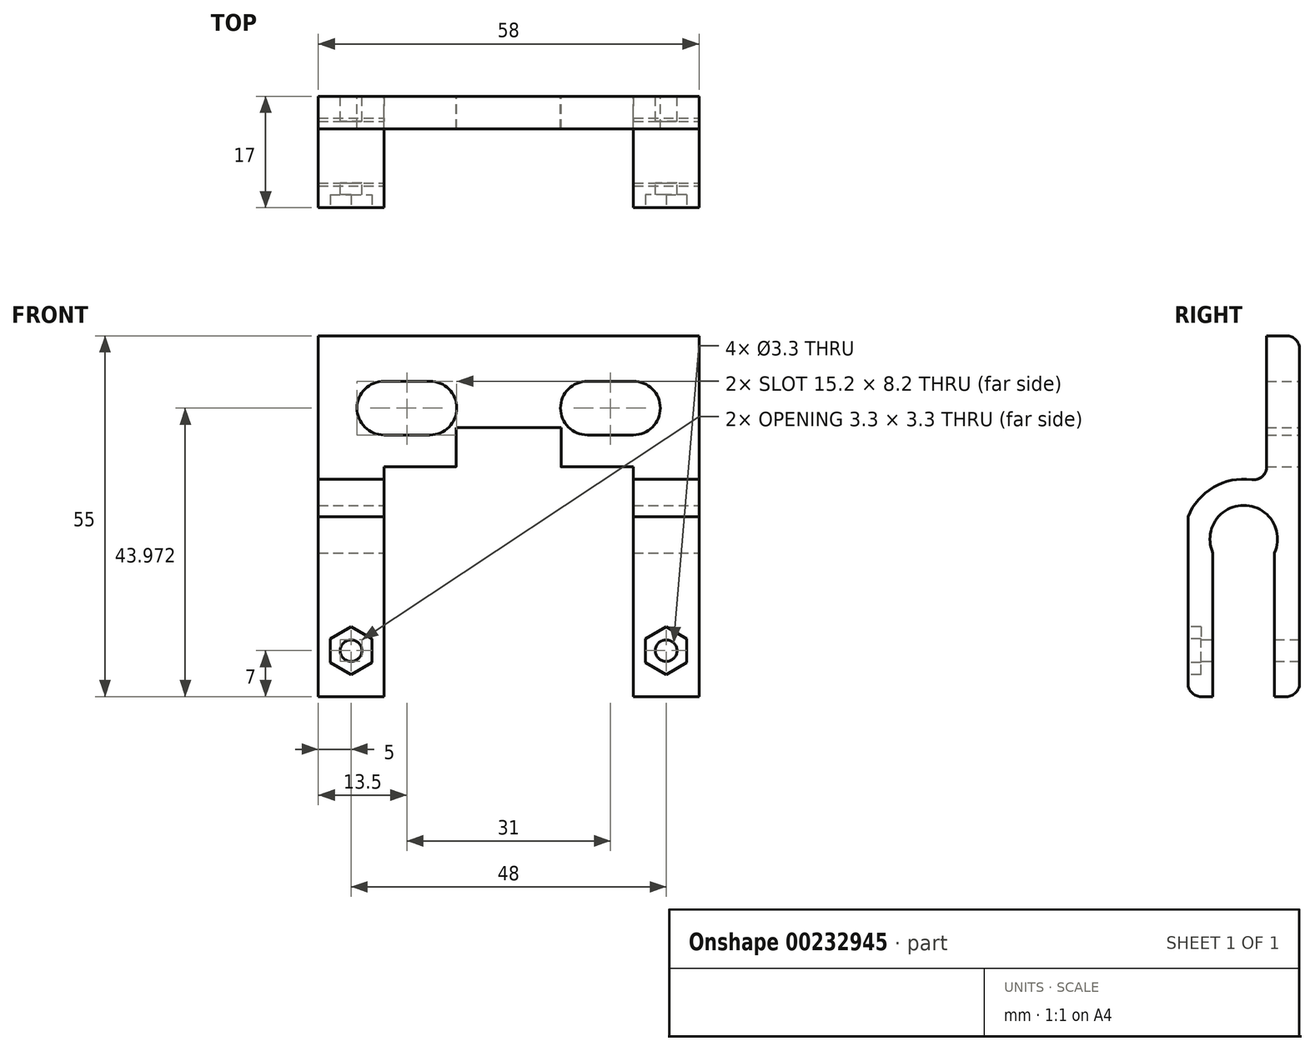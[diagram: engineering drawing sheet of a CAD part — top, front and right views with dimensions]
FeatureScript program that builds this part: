
annotation { "Feature Type Name" : "Feature", "Feature Type Description" : "" }
export const myFeature = defineFeature(function(context is Context, id is Id, definition is map)
    precondition{}
    {
        {
            var Q0;
            Q0=qCreatedBy(makeId("Front.planeOp"),FACE);
            var sketch = newSketch(context, id + "F0", { "sketchPlane" : qUnion([Q0])});
            skLineSegment(sketch, "E0.bottom", {"start": v(-13, -25) * mm, "end": v(-3, -25) * mm});
            skLineSegment(sketch, "E0.left", {"start": v(-13, -25) * mm, "end": v(-13, 25) * mm});
            skLineSegment(sketch, "E1", {"start": v(-3, -25) * mm, "end": v(-3, -5) * mm});
            skLineSegment(sketch, "E2", {"start": v(35, -5) * mm, "end": v(35, -25) * mm});
            skLineSegment(sketch, "E3", {"start": v(35, -25) * mm, "end": v(45, -25) * mm});
            skLineSegment(sketch, "E4", {"start": v(45, -25) * mm, "end": v(45, 25) * mm});
            skLineSegment(sketch, "E5", {"start": v(45, 25) * mm, "end": v(45, 30) * mm});
            skLineSegment(sketch, "E6", {"start": v(45, 30) * mm, "end": v(-13, 30) * mm});
            skLineSegment(sketch, "E7", {"start": v(-13, 30) * mm, "end": v(-13, 25) * mm});
            skLineSegment(sketch, "E8", {"start": v(-3, -5) * mm, "end": v(-3, 0) * mm});
            skLineSegment(sketch, "E9", {"start": v(35, 0) * mm, "end": v(35, -5) * mm});
            skLineSegment(sketch, "E10", {"start": v(-13, 30) * mm, "end": v(-13, 18.97) * mm});
            skPoint(sketch, "E11", {"position": v(4, 18.97) * mm});
            skPoint(sketch, "E12", {"position": v(28, 18.97) * mm});
            skArc(sketch, "E13", {"start": v(28, 23.07) * mm, "mid": v(23.9, 18.97) * mm, "end": v(28, 14.87) * mm});
            skArc(sketch, "E14", {"start": v(-3, 23.07) * mm, "mid": v(-7.1, 18.97) * mm, "end": v(-3, 14.87) * mm});
            skArc(sketch, "E15", {"start": v(35, 14.87) * mm, "mid": v(39.1, 18.97) * mm, "end": v(35, 23.07) * mm});
            skLineSegment(sketch, "E16", {"start": v(4, 14.87) * mm, "end": v(-3, 14.87) * mm});
            skLineSegment(sketch, "E17", {"start": v(-3, 23.07) * mm, "end": v(4, 23.07) * mm});
            skLineSegment(sketch, "E18", {"start": v(28, 14.87) * mm, "end": v(35, 14.87) * mm});
            skLineSegment(sketch, "E19", {"start": v(28, 23.07) * mm, "end": v(35, 23.07) * mm});
            skPoint(sketch, "E20.trimOffspring.end.orphan", {"position": v(45, 18.97) * mm});
            skLineSegment(sketch, "E21", {"start": v(-8, -25) * mm, "end": v(-8, -18) * mm});
            skLineSegment(sketch, "E22", {"start": v(40, -25) * mm, "end": v(40, -18) * mm});
            skCircle(sketch, "E23", {"center": v(40, -18) * mm, "radius": 1.65 * mm});
            skCircle(sketch, "E24", {"center": v(-8, -18) * mm, "radius": 1.65 * mm});
            skCircle(sketch, "E25.cCircle", {"center": v(-8, -18) * mm, "radius": 3.1 * mm, "construction": true});
            skLineSegment(sketch, "E25.0", {"start": v(-4.9, -16.21) * mm, "end": v(-4.9, -19.79) * mm});
            skLineSegment(sketch, "E25.1", {"start": v(-4.9, -19.79) * mm, "end": v(-8, -21.58) * mm});
            skLineSegment(sketch, "E25.2", {"start": v(-8, -21.58) * mm, "end": v(-11.1, -19.79) * mm});
            skLineSegment(sketch, "E25.3", {"start": v(-11.1, -19.79) * mm, "end": v(-11.1, -16.21) * mm});
            skLineSegment(sketch, "E25.4", {"start": v(-11.1, -16.21) * mm, "end": v(-8, -14.42) * mm});
            skLineSegment(sketch, "E25.5", {"start": v(-8, -14.42) * mm, "end": v(-4.9, -16.21) * mm});
            skPoint(sketch, "E25.0.midPoint", {"position": v(-4.9, -18) * mm});
            skCircle(sketch, "E26.cCircle", {"center": v(40, -18) * mm, "radius": 3.1 * mm, "construction": true});
            skLineSegment(sketch, "E26.0", {"start": v(36.9, -19.79) * mm, "end": v(36.9, -16.21) * mm});
            skLineSegment(sketch, "E26.1", {"start": v(36.9, -16.21) * mm, "end": v(40, -14.42) * mm});
            skLineSegment(sketch, "E26.2", {"start": v(40, -14.42) * mm, "end": v(43.1, -16.21) * mm});
            skLineSegment(sketch, "E26.3", {"start": v(43.1, -16.21) * mm, "end": v(43.1, -19.79) * mm});
            skLineSegment(sketch, "E26.4", {"start": v(43.1, -19.79) * mm, "end": v(40, -21.58) * mm});
            skLineSegment(sketch, "E26.5", {"start": v(40, -21.58) * mm, "end": v(36.9, -19.79) * mm});
            skPoint(sketch, "E26.0.midPoint", {"position": v(36.9, -18) * mm});
            skLineSegment(sketch, "E27", {"start": v(-3, 0) * mm, "end": v(-3, 5) * mm});
            skLineSegment(sketch, "E28", {"start": v(35, 5) * mm, "end": v(35, 0) * mm});
            skLineSegment(sketch, "E29", {"start": v(35, 0) * mm, "end": v(35, 10) * mm});
            skLineSegment(sketch, "E30", {"start": v(35, 10) * mm, "end": v(24, 10) * mm});
            skLineSegment(sketch, "E31", {"start": v(-3, 10) * mm, "end": v(-3, 5) * mm});
            skLineSegment(sketch, "E32", {"start": v(24, 10) * mm, "end": v(24, 16) * mm});
            skLineSegment(sketch, "E33", {"start": v(8, 10) * mm, "end": v(8, 16) * mm});
            skLineSegment(sketch, "E34.trimOffspring", {"start": v(24, 16) * mm, "end": v(8, 16) * mm});
            skArc(sketch, "E35", {"start": v(4, 14.87) * mm, "mid": v(8.1, 18.97) * mm, "end": v(4, 23.07) * mm});
            skLineSegment(sketch, "E36.trimOffspring", {"start": v(8, 10) * mm, "end": v(-3, 10) * mm});
            skSolve(sketch);
        }
        {
            var Q0;
            Q0=makeQuery(id+"F0.imprint","IMPRINT",FACE,{"disambiguationData":[TD([[makeQuery(id+"F0.imprint","IMPRINT",EDGE,{"derivedFrom":sQuery(id+"F0.wireOp",EDGE,"E0.left")}),-1.0]])]});
            var Q1;
            Q1=makeQuery(id+"F0.imprint","IMPRINT",FACE,{"disambiguationData":[TD([[makeQuery(id+"F0.imprint","IMPRINT",EDGE,{"derivedFrom":sQuery(id+"F0.wireOp",EDGE,"E23")}),-1.0]])]});
            var Q2;
            Q2=makeQuery(id+"F0.imprint","IMPRINT",FACE,{"disambiguationData":[TD([[makeQuery(id+"F0.imprint","IMPRINT",EDGE,{"derivedFrom":sQuery(id+"F0.wireOp",EDGE,"E24")}),-1.0]])]});
            extrude(context, id + "F1", {"entities" : qUnion([Q0, Q1, Q2]), "depth" : 17 * mm});
        }
        {
            var Q0;
            Q0=makeQuery(id+"F1.opExtrude","SWEPT_FACE",FACE,{"disambiguationData":[OSD([sQuery(id+"F0.wireOp",EDGE,"E4")])]});
            var sketch = newSketch(context, id + "F2", { "sketchPlane" : qUnion([Q0])});
            skArc(sketch, "E37", {"start": v(-3.8, -3.1) * mm, "mid": v(-8.5, 4.15) * mm, "end": v(-13.2, -3.1) * mm});
            skLineSegment(sketch, "E38", {"start": v(-17, -25) * mm, "end": v(-13.2, -25) * mm});
            skLineSegment(sketch, "E39", {"start": v(0, -25) * mm, "end": v(-3.8, -25) * mm});
            skLineSegment(sketch, "E40", {"start": v(-13.2, -25) * mm, "end": v(-13.2, -3.1) * mm});
            skLineSegment(sketch, "E41", {"start": v(-3.8, -25) * mm, "end": v(-3.8, -3.1) * mm});
            skPoint(sketch, "E42.start.orphan", {"position": v(-8.5, -25) * mm});
            skArc(sketch, "E43.0", {"start": v(-5, 7.45) * mm, "mid": v(-12.06, 7.43) * mm, "end": v(-17, 2.39) * mm});
            skPoint(sketch, "E44", {"position": v(-17, 2.39) * mm});
            skLineSegment(sketch, "E45", {"start": v(0, -25) * mm, "end": v(-4, -25) * mm});
            skLineSegment(sketch, "E46", {"start": v(0, 30) * mm, "end": v(-5, 30) * mm});
            skLineSegment(sketch, "E47", {"start": v(-5, 30) * mm, "end": v(-5, 7.45) * mm});
            skPoint(sketch, "E48", {"position": v(0, 18.99) * mm});
            skSolve(sketch);
        }
        {
            var Q0;
            {var subQ0=sQuery(id+"F2.wireOp",EDGE,"E43.0");Q0=makeQuery(id+"F2.imprint","IMPRINT",FACE,{"disambiguationData":[TD([[makeQuery(id+"F2.imprint","IMPRINT",EDGE,{"derivedFrom":subQ0}),-1.0]])]});}
            var Q1;
            Q1=makeQuery(id+"F2.imprint","IMPRINT",FACE,{"disambiguationData":[TD([[makeQuery(id+"F2.imprint","IMPRINT",EDGE,{"derivedFrom":sQuery(id+"F2.wireOp",EDGE,"E37")}),1.0]])]});
            extrude(context, id + "F3", {"entities" : qUnion([Q0, Q1]), "operationType" : NewBodyOperationType.REMOVE, "oppositeDirection" : true, "depth" : 80 * mm});
        }
        {
            var Q0;
            Q0=makeQuery(id+"F3.boolean.opBoolean","COPY",EDGE,{"derivedFrom":makeQuery(id+"F3.opExtrude","SWEPT_EDGE",EDGE,{"disambiguationData":[OSD([sQuery(id+"F0.wireOp",EDGE,"E5"),sQuery(id+"F0.wireOp",EDGE,"E6"),sQuery(id+"F2.wireOp",EDGE,"E46"),sQuery(id+"F2.wireOp",EDGE,"E47")])]})});
            var Q1;
            Q1=makeQuery(id+"F1.opExtrude","CAP_EDGE",EDGE,{"disambiguationData":[OSD([sQuery(id+"F0.wireOp",EDGE,"E6")])],"isStart":true});
            var Q2;
            Q2=makeQuery(id+"F1.opExtrude","CAP_EDGE",EDGE,{"disambiguationData":[OSD([sQuery(id+"F0.wireOp",EDGE,"E3")])],"isStart":false});
            var Q3;
            {var subQ0=sQuery(id+"F0.wireOp",EDGE,"E3");var subQ1=sQuery(id+"F2.wireOp",EDGE,"E40");Q3=makeQuery(id+"F3.boolean.opBoolean","COPY",EDGE,{"disambiguationData":[topologyDisambiguationEdgeConnected([makeQuery(id+"F1.opExtrude","SWEPT_FACE",FACE,{"disambiguationData":[OSD([subQ0])]})])],"derivedFrom":makeQuery(id+"F3.opExtrude","SWEPT_EDGE",EDGE,{"disambiguationData":[OSD([subQ0,sQuery(id+"F0.wireOp",EDGE,"E4"),sQuery(id+"F2.wireOp",EDGE,"E38"),subQ1])]})});}
            var Q4;
            {var subQ0=sQuery(id+"F2.wireOp",EDGE,"E41");Q4=makeQuery(id+"F3.boolean.opBoolean","COPY",EDGE,{"disambiguationData":[topologyDisambiguationEdgeConnected([makeQuery(id+"F1.opExtrude","SWEPT_FACE",FACE,{"disambiguationData":[OSD([sQuery(id+"F0.wireOp",EDGE,"E3")])]})])],"derivedFrom":makeQuery(id+"F3.opExtrude","SWEPT_EDGE",EDGE,{"disambiguationData":[OSD([subQ0,sQuery(id+"F2.wireOp",EDGE,"E45")])]})});}
            var Q5;
            Q5=makeQuery(id+"F1.opExtrude","CAP_EDGE",EDGE,{"disambiguationData":[OSD([sQuery(id+"F0.wireOp",EDGE,"E3")])],"isStart":true});
            var Q6;
            Q6=makeQuery(id+"F1.opExtrude","CAP_EDGE",EDGE,{"disambiguationData":[OSD([sQuery(id+"F0.wireOp",EDGE,"E0.bottom")])],"isStart":false});
            var Q7;
            {var subQ0=sQuery(id+"F2.wireOp",EDGE,"E40");Q7=makeQuery(id+"F3.boolean.opBoolean","COPY",EDGE,{"disambiguationData":[topologyDisambiguationEdgeConnected([makeQuery(id+"F1.opExtrude","SWEPT_FACE",FACE,{"disambiguationData":[OSD([sQuery(id+"F0.wireOp",EDGE,"E0.bottom")])]})])],"derivedFrom":makeQuery(id+"F3.opExtrude","SWEPT_EDGE",EDGE,{"disambiguationData":[OSD([sQuery(id+"F0.wireOp",EDGE,"E3"),sQuery(id+"F0.wireOp",EDGE,"E4"),sQuery(id+"F2.wireOp",EDGE,"E38"),subQ0])]})});}
            var Q8;
            {var subQ0=sQuery(id+"F2.wireOp",EDGE,"E41");Q8=makeQuery(id+"F3.boolean.opBoolean","COPY",EDGE,{"disambiguationData":[topologyDisambiguationEdgeConnected([makeQuery(id+"F1.opExtrude","SWEPT_FACE",FACE,{"disambiguationData":[OSD([sQuery(id+"F0.wireOp",EDGE,"E0.bottom")])]})])],"derivedFrom":makeQuery(id+"F3.opExtrude","SWEPT_EDGE",EDGE,{"disambiguationData":[OSD([subQ0,sQuery(id+"F2.wireOp",EDGE,"E45")])]})});}
            var Q9;
            Q9=makeQuery(id+"F1.opExtrude","CAP_EDGE",EDGE,{"disambiguationData":[OSD([sQuery(id+"F0.wireOp",EDGE,"E0.bottom")])],"isStart":true});
            var Q10;
            Q10=makeQuery(id+"F3.boolean.opBoolean","COPY",EDGE,{"derivedFrom":makeQuery(id+"F3.opExtrude","SWEPT_EDGE",EDGE,{"disambiguationData":[OSD([sQuery(id+"F2.wireOp",EDGE,"E43.0"),sQuery(id+"F2.wireOp",EDGE,"E47")])]})});
            fillet(context, id + "F4", {"entities" : qUnion([Q0, Q1, Q2, Q3, Q4, Q5, Q6, Q7, Q8, Q9, Q10]), "radius" : 2 * mm, "tangentPropagation" : true, "allowEdgeOverflow" : false});
        }
        {
            var Q0;
            Q0=makeQuery(id+"F1.opExtrude","CAP_FACE",FACE,{"disambiguationData":[OSD([sQuery(id+"F0.wireOp",EDGE,"E0.left"),sQuery(id+"F0.wireOp",EDGE,"E0.bottom"),sQuery(id+"F0.wireOp",EDGE,"E1"),sQuery(id+"F0.wireOp",EDGE,"E2"),sQuery(id+"F0.wireOp",EDGE,"E3"),sQuery(id+"F0.wireOp",EDGE,"E4"),sQuery(id+"F0.wireOp",EDGE,"E5"),sQuery(id+"F0.wireOp",EDGE,"E6"),sQuery(id+"F0.wireOp",EDGE,"E8"),sQuery(id+"F0.wireOp",EDGE,"RMU9ffyy-MDxI-VZhF-XVax-glMUIUJa8zU6"),sQuery(id+"F0.wireOp",EDGE,"95sGthqd-6ktj-8Q6e-P4ge-x4HrphV32gUs"),sQuery(id+"F0.wireOp",EDGE,"E9"),sQuery(id+"F0.wireOp",EDGE,"E10"),sQuery(id+"F0.wireOp",EDGE,"JnmtOXyl-UYW7-4xJe-bdZV-FBQ4210GDwAH"),sQuery(id+"F0.wireOp",EDGE,"E13"),sQuery(id+"F0.wireOp",EDGE,"E14"),sQuery(id+"F0.wireOp",EDGE,"E15"),sQuery(id+"F0.wireOp",EDGE,"E16"),sQuery(id+"F0.wireOp",EDGE,"E17"),sQuery(id+"F0.wireOp",EDGE,"E18"),sQuery(id+"F0.wireOp",EDGE,"E19"),sQuery(id+"F0.wireOp",EDGE,"E23"),sQuery(id+"F0.wireOp",EDGE,"E24")])],"isStart":false});
            var sketch = newSketch(context, id + "F5", { "sketchPlane" : qUnion([Q0])});
            skCircle(sketch, "E49.cCircle", {"center": v(-8, -18) * mm, "radius": 3.15 * mm, "construction": true});
            skLineSegment(sketch, "E49.0", {"start": v(-4.85, -16.18) * mm, "end": v(-4.85, -19.82) * mm});
            skLineSegment(sketch, "E49.1", {"start": v(-4.85, -19.82) * mm, "end": v(-8, -21.64) * mm});
            skLineSegment(sketch, "E49.2", {"start": v(-8, -21.64) * mm, "end": v(-11.15, -19.82) * mm});
            skLineSegment(sketch, "E49.3", {"start": v(-11.15, -19.82) * mm, "end": v(-11.15, -16.18) * mm});
            skLineSegment(sketch, "E49.4", {"start": v(-11.15, -16.18) * mm, "end": v(-8, -14.36) * mm});
            skLineSegment(sketch, "E49.5", {"start": v(-8, -14.36) * mm, "end": v(-4.85, -16.18) * mm});
            skPoint(sketch, "E49.0.midPoint", {"position": v(-4.85, -18) * mm});
            skCircle(sketch, "E50.cCircle", {"center": v(40, -18) * mm, "radius": 3.15 * mm, "construction": true});
            skLineSegment(sketch, "E50.0", {"start": v(36.85, -19.82) * mm, "end": v(36.85, -16.18) * mm});
            skLineSegment(sketch, "E50.1", {"start": v(36.85, -16.18) * mm, "end": v(40, -14.36) * mm});
            skLineSegment(sketch, "E50.2", {"start": v(40, -14.36) * mm, "end": v(43.15, -16.18) * mm});
            skLineSegment(sketch, "E50.3", {"start": v(43.15, -16.18) * mm, "end": v(43.15, -19.82) * mm});
            skLineSegment(sketch, "E50.4", {"start": v(43.15, -19.82) * mm, "end": v(40, -21.64) * mm});
            skLineSegment(sketch, "E50.5", {"start": v(40, -21.64) * mm, "end": v(36.85, -19.82) * mm});
            skPoint(sketch, "E50.0.midPoint", {"position": v(36.85, -18) * mm});
            skSolve(sketch);
        }
        {
            var Q0;
            Q0=makeQuery(id+"F5.imprint","IMPRINT",FACE,{"disambiguationData":[TD([[makeQuery(id+"F5.imprint","IMPRINT",EDGE,{"derivedFrom":sQuery(id+"F5.wireOp",EDGE,"E49.0")}),-1.0]])]});
            var Q1;
            Q1=makeQuery(id+"F5.imprint","IMPRINT",FACE,{"disambiguationData":[TD([[makeQuery(id+"F5.imprint","IMPRINT",EDGE,{"derivedFrom":sQuery(id+"F5.wireOp",EDGE,"E50.0")}),-1.0]])]});
            extrude(context, id + "F6", {"entities" : qUnion([Q0, Q1]), "operationType" : NewBodyOperationType.REMOVE, "oppositeDirection" : true, "depth" : 2 * mm});
        }
    });
